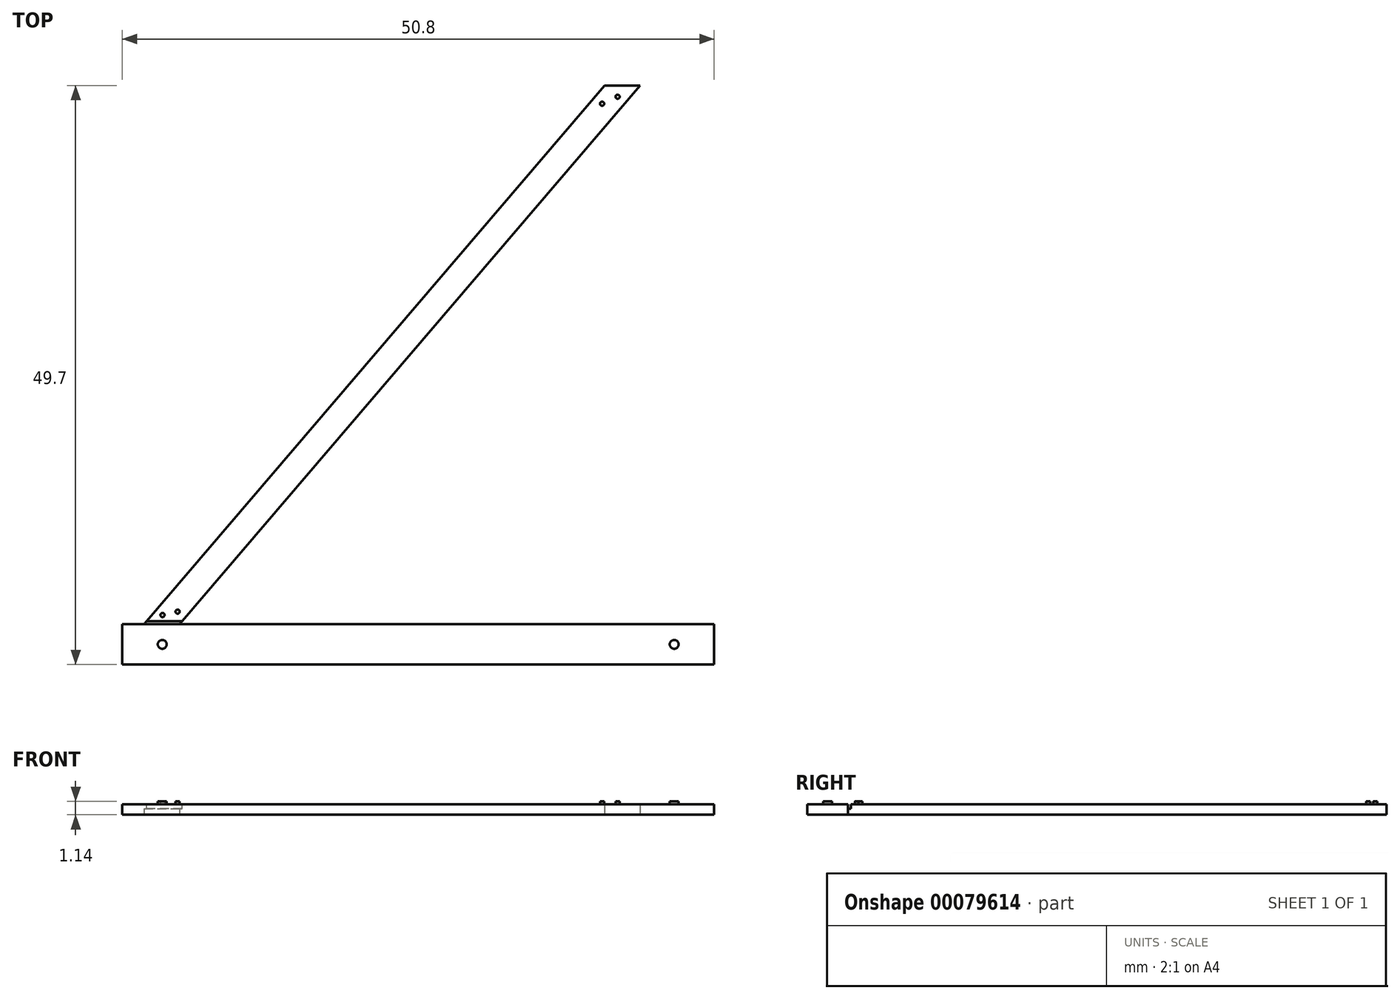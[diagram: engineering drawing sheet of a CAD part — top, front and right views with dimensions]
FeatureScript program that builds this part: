
annotation { "Feature Type Name" : "Feature", "Feature Type Description" : "" }
export const myFeature = defineFeature(function(context is Context, id is Id, definition is map)
    precondition{}
    {
        {
            var Q0;
            Q0=qCreatedBy(makeId("Top.planeOp"),FACE);
            var sketch = newSketch(context, id + "F0", { "sketchPlane" : qUnion([Q0])});
            skLineSegment(sketch, "E0.bottom", {"start": v(-26.81, -12.22) * mm, "end": v(-24.95, -12.22) * mm});
            skLineSegment(sketch, "E0.top", {"start": v(-26.81, -15.7) * mm, "end": v(23.99, -15.7) * mm});
            skLineSegment(sketch, "E0.left", {"start": v(-26.81, -12.22) * mm, "end": v(-26.81, -15.7) * mm});
            skLineSegment(sketch, "E0.right", {"start": v(23.99, -12.22) * mm, "end": v(23.99, -15.7) * mm});
            skLineSegment(sketch, "E1", {"start": v(-24.95, -12.22) * mm, "end": v(14.59, 34.01) * mm});
            skLineSegment(sketch, "E2", {"start": v(-21.9, -12.22) * mm, "end": v(17.64, 34.01) * mm});
            skLineSegment(sketch, "E3", {"start": v(14.59, 34.01) * mm, "end": v(17.64, 34.01) * mm});
            skLineSegment(sketch, "E4.trimOffspring", {"start": v(-21.9, -12.22) * mm, "end": v(23.99, -12.22) * mm});
            skSolve(sketch);
        }
        {
            var Q0;
            Q0 = qSketchRegion(id + "F0", true);
            extrude(context, id + "F1", {"entities" : qUnion([Q0]), "depth" : 0.89 * mm});
        }
        {
            var Q0;
            Q0=makeQuery(id+"F1.opExtrude","CAP_FACE",FACE,{"disambiguationData":[OSD([sQuery(id+"F0.wireOp",EDGE,"E0.bottom"),sQuery(id+"F0.wireOp",EDGE,"E0.top"),sQuery(id+"F0.wireOp",EDGE,"E0.left"),sQuery(id+"F0.wireOp",EDGE,"E0.right"),sQuery(id+"F0.wireOp",EDGE,"E1"),sQuery(id+"F0.wireOp",EDGE,"E2"),sQuery(id+"F0.wireOp",EDGE,"E3"),sQuery(id+"F0.wireOp",EDGE,"E4.trimOffspring")])],"isStart":false});
            var sketch = newSketch(context, id + "F2", { "sketchPlane" : qUnion([Q0])});
            skLineSegment(sketch, "E5", {"start": v(-24.95, -12.22) * mm, "end": v(-21.9, -12.22) * mm});
            skLineSegment(sketch, "E6", {"start": v(-21.9, -12.22) * mm, "end": v(-21.68, -11.96) * mm});
            skLineSegment(sketch, "E7", {"start": v(-21.68, -11.96) * mm, "end": v(-24.73, -11.96) * mm});
            skLineSegment(sketch, "E8", {"start": v(-24.73, -11.96) * mm, "end": v(-24.95, -12.22) * mm});
            skSolve(sketch);
        }
        {
            var Q0;
            Q0 = qSketchRegion(id + "F2", true);
            extrude(context, id + "F3", {"entities" : qUnion([Q0]), "operationType" : NewBodyOperationType.REMOVE, "oppositeDirection" : true, "depth" : 0.38 * mm});
        }
        {
            var Q0;
            {var subQ0=sQuery(id+"F0.wireOp",EDGE,"E1");var subQ1=sQuery(id+"F0.wireOp",EDGE,"E2");var subQ2=sQuery(id+"F0.wireOp",EDGE,"E3");Q0=makeQuery(id+"F3.boolean.opBoolean","SPLIT",FACE,{"disambiguationData":[TD([makeQuery(id+"F1.opExtrude","SWEPT_FACE",FACE,{"disambiguationData":[OSD([subQ0])]})])],"derivedFrom":makeQuery(id+"F1.opExtrude","CAP_FACE",FACE,{"disambiguationData":[OSD([sQuery(id+"F0.wireOp",EDGE,"E0.bottom"),sQuery(id+"F0.wireOp",EDGE,"E0.top"),sQuery(id+"F0.wireOp",EDGE,"E0.left"),sQuery(id+"F0.wireOp",EDGE,"E0.right"),subQ0,subQ1,subQ2,sQuery(id+"F0.wireOp",EDGE,"E4.trimOffspring")])],"isStart":false})});}
            var sketch = newSketch(context, id + "F4", { "sketchPlane" : qUnion([Q0])});
            skCircle(sketch, "E9", {"center": v(-23.36, -11.44) * mm, "radius": 0.18 * mm});
            skCircle(sketch, "E10", {"center": v(-22.07, -11.14) * mm, "radius": 0.18 * mm});
            skCircle(sketch, "E11", {"center": v(-23.38, -13.95) * mm, "radius": 0.38 * mm});
            skCircle(sketch, "E12", {"center": v(15.7, 33.05) * mm, "radius": 0.18 * mm});
            skCircle(sketch, "E13", {"center": v(14.37, 32.45) * mm, "radius": 0.18 * mm});
            skCircle(sketch, "E14", {"center": v(20.56, -13.95) * mm, "radius": 0.38 * mm});
            skSolve(sketch);
        }
        {
            var Q0;
            Q0 = qSketchRegion(id + "F4", true);
            extrude(context, id + "F5", {"entities" : qUnion([Q0]), "operationType" : NewBodyOperationType.ADD, "depth" : 0.25 * mm});
        }
    });
